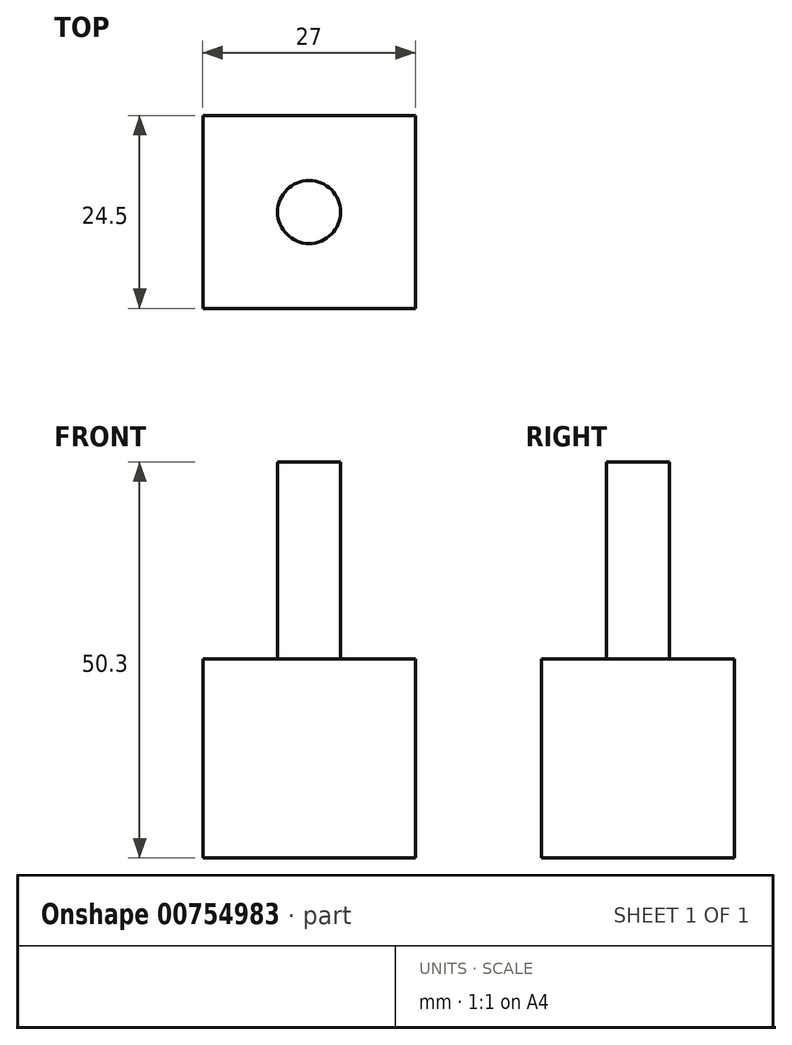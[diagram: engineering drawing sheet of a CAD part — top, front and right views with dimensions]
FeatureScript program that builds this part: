
annotation { "Feature Type Name" : "Feature", "Feature Type Description" : "" }
export const myFeature = defineFeature(function(context is Context, id is Id, definition is map)
    precondition{}
    {
        {
            var Q0;
            Q0=qCreatedBy(makeId("Top.planeOp"),FACE);
            var sketch = newSketch(context, id + "F0", { "sketchPlane" : qUnion([Q0])});
            skLineSegment(sketch, "E0.bottom", {"start": v(-11.9, 4.56) * mm, "end": v(15.1, 4.56) * mm});
            skLineSegment(sketch, "E0.top", {"start": v(-11.9, -19.94) * mm, "end": v(15.1, -19.94) * mm});
            skLineSegment(sketch, "E0.left", {"start": v(-11.9, 4.56) * mm, "end": v(-11.9, -19.94) * mm});
            skLineSegment(sketch, "E0.right", {"start": v(15.1, 4.56) * mm, "end": v(15.1, -19.94) * mm});
            skSolve(sketch);
        }
        {
            var Q0;
            Q0 = qSketchRegion(id + "F0", true);
            extrude(context, id + "F1", {"entities" : qUnion([Q0]), "depth" : 25.3 * mm, "offsetDistance" : 25 * mm});
        }
        {
            var Q0;
            Q0=makeQuery(id+"F1.opExtrude","CAP_FACE",FACE,{"disambiguationData":[OSD([sQuery(id+"F0.wireOp",EDGE,"E0.bottom"),sQuery(id+"F0.wireOp",EDGE,"E0.top"),sQuery(id+"F0.wireOp",EDGE,"E0.left"),sQuery(id+"F0.wireOp",EDGE,"E0.right")])],"isStart":false});
            var sketch = newSketch(context, id + "F2", { "sketchPlane" : qUnion([Q0])});
            skCircle(sketch, "E1", {"center": v(1.6, -7.69) * mm, "radius": 4 * mm});
            skPoint(sketch, "E1.centerSnap0", {"position": v(1.6, -19.94) * mm});
            skPoint(sketch, "E1.centerSnap1", {"position": v(15.1, -7.69) * mm});
            skSolve(sketch);
        }
        {
            var Q0;
            Q0 = qSketchRegion(id + "F2", true);
            extrude(context, id + "F3", {"entities" : qUnion([Q0]), "operationType" : NewBodyOperationType.ADD, "depth" : 25 * mm, "offsetDistance" : 25 * mm});
        }
    });
